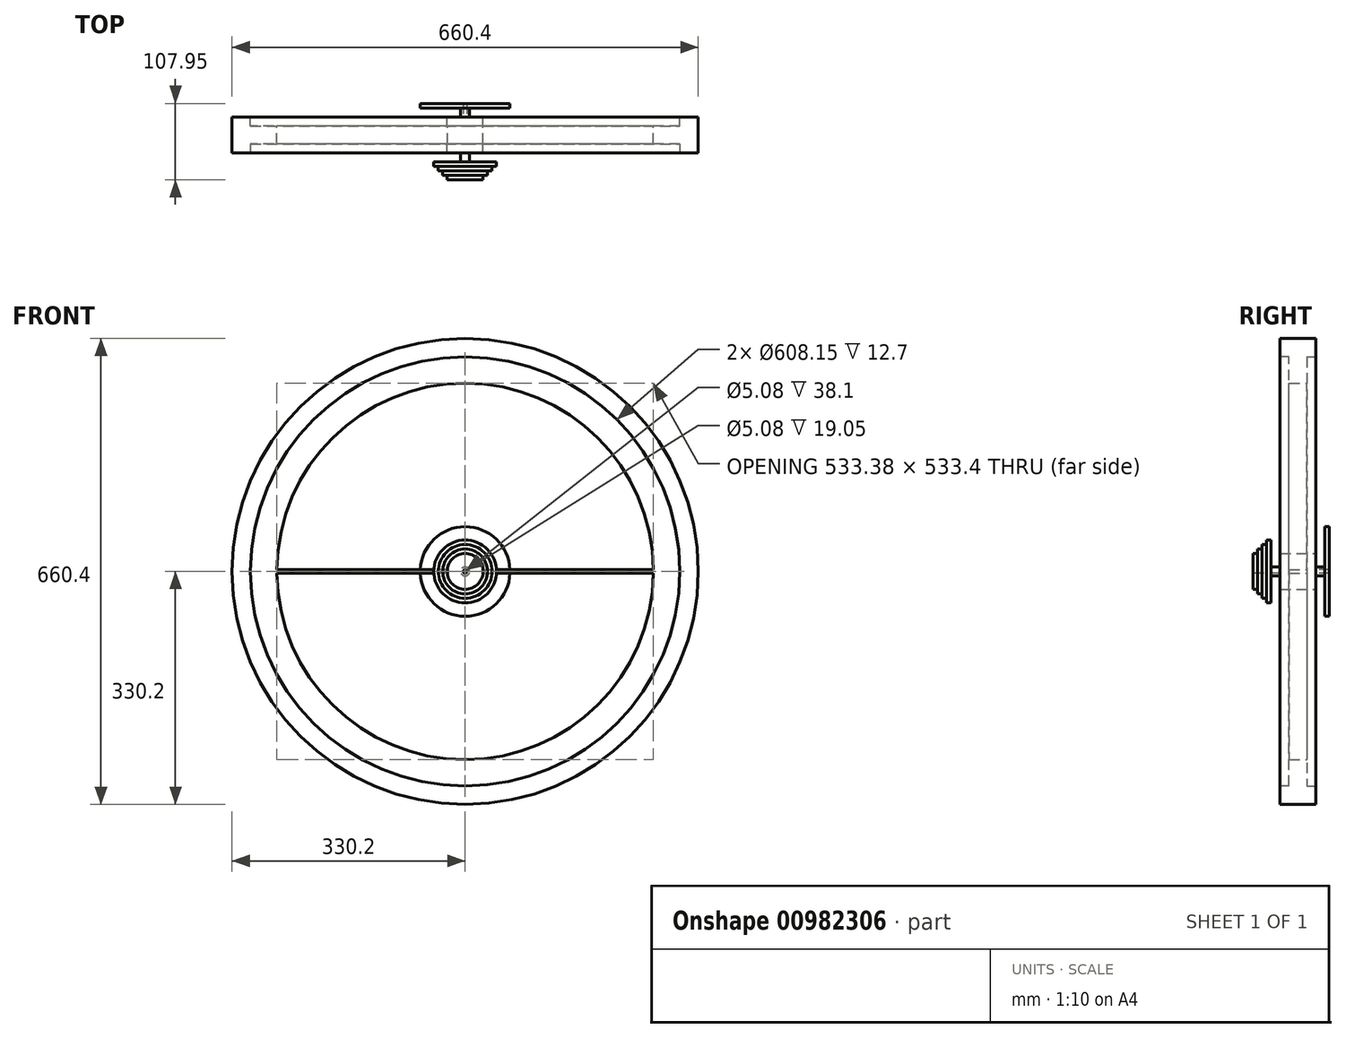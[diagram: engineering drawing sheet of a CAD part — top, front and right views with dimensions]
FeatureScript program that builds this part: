
annotation { "Feature Type Name" : "Feature", "Feature Type Description" : "" }
export const myFeature = defineFeature(function(context is Context, id is Id, definition is map)
    precondition{}
    {
        {
            var Q0;
            Q0=qCreatedBy(makeId("Front.planeOp"),FACE);
            var sketch = newSketch(context, id + "F0", { "sketchPlane" : qUnion([Q0])});
            skCircle(sketch, "E0", {"center": v(0, 0) * mm, "radius": 330.2 * mm});
            skCircle(sketch, "E1", {"center": v(0, 0) * mm, "radius": 266.7 * mm});
            skSolve(sketch);
        }
        {
            var Q0;
            Q0=makeQuery(id+"F0.imprint","IMPRINT",FACE,{"disambiguationData":[TD([[makeQuery(id+"F0.imprint","IMPRINT",EDGE,{"derivedFrom":sQuery(id+"F0.wireOp",EDGE,"E0")}),1.0]])]});
            extrude(context, id + "F1", {"entities" : qUnion([Q0]), "depth" : 25.4 * mm, "offsetDistance" : 25.4 * mm, "hasSecondDirection" : true, "secondDirectionOppositeDirection" : true, "secondDirectionDepth" : 25.4 * mm});
        }
        {
            var Q0;
            Q0=makeQuery(id+"F1.opExtrude","CAP_FACE",FACE,{"disambiguationData":[OSD([sQuery(id+"F0.wireOp",EDGE,"E0"),sQuery(id+"F0.wireOp",EDGE,"E1")])],"isStart":false});
            cPlane(context, id + "F2", {"entities" : qUnion([Q0]), "cplaneType" : CPlaneType.OFFSET, "offset" : 12.7 * mm, "width" : 152.4 * mm, "height" : 152.4 * mm});
        }
        {
            var Q0;
            Q0=qCreatedBy(id+"F2.planeOp",FACE);
            var sketch = newSketch(context, id + "F3", { "sketchPlane" : qUnion([Q0])});
            skPoint(sketch, "E2.0", {"position": v(0, 0) * mm});
            skCircle(sketch, "E3", {"center": v(0, 0) * mm, "radius": 44.45 * mm});
            skCircle(sketch, "E4", {"center": v(0, 0) * mm, "radius": 38.1 * mm});
            skCircle(sketch, "E5", {"center": v(0, 0) * mm, "radius": 31.75 * mm});
            skCircle(sketch, "E6", {"center": v(0, 0) * mm, "radius": 25.4 * mm});
            skCircle(sketch, "E7", {"center": v(0, 0) * mm, "radius": 19.05 * mm});
            skCircle(sketch, "E8", {"center": v(0, 0) * mm, "radius": 6.35 * mm});
            skSolve(sketch);
        }
        {
            var Q0;
            Q0=makeQuery(id+"F3.imprint","IMPRINT",FACE,{"disambiguationData":[TD([[makeQuery(id+"F3.imprint","IMPRINT",EDGE,{"derivedFrom":sQuery(id+"F3.wireOp",EDGE,"E3")}),1.0]])]});
            extrude(context, id + "F4", {"entities" : qUnion([Q0]), "depth" : 6.35 * mm, "offsetDistance" : 25.4 * mm});
        }
        {
            var Q0;
            Q0=makeQuery(id+"F3.imprint","IMPRINT",FACE,{"disambiguationData":[TD([[makeQuery(id+"F3.imprint","IMPRINT",EDGE,{"derivedFrom":sQuery(id+"F3.wireOp",EDGE,"E4")}),1.0]])]});
            extrude(context, id + "F5", {"entities" : qUnion([Q0]), "operationType" : NewBodyOperationType.ADD, "depth" : 12.7 * mm, "offsetDistance" : 25.4 * mm});
        }
        {
            var Q0;
            Q0=makeQuery(id+"F3.imprint","IMPRINT",FACE,{"disambiguationData":[TD([[makeQuery(id+"F3.imprint","IMPRINT",EDGE,{"derivedFrom":sQuery(id+"F3.wireOp",EDGE,"E5")}),1.0]])]});
            extrude(context, id + "F6", {"entities" : qUnion([Q0]), "operationType" : NewBodyOperationType.ADD, "depth" : 19.05 * mm, "offsetDistance" : 25.4 * mm});
        }
        {
            var Q0;
            Q0=makeQuery(id+"F3.imprint","IMPRINT",FACE,{"disambiguationData":[TD([[makeQuery(id+"F3.imprint","IMPRINT",EDGE,{"derivedFrom":sQuery(id+"F3.wireOp",EDGE,"E6")}),1.0]])]});
            extrude(context, id + "F7", {"entities" : qUnion([Q0]), "operationType" : NewBodyOperationType.ADD, "depth" : 25.4 * mm, "offsetDistance" : 25.4 * mm});
        }
        {
            var Q0;
            Q0=makeQuery(id+"F1.opExtrude","CAP_FACE",FACE,{"disambiguationData":[OSD([sQuery(id+"F0.wireOp",EDGE,"E0"),sQuery(id+"F0.wireOp",EDGE,"E1")])],"isStart":true});
            cPlane(context, id + "F8", {"entities" : qUnion([Q0]), "cplaneType" : CPlaneType.OFFSET, "offset" : 12.7 * mm, "width" : 152.4 * mm, "height" : 152.4 * mm});
        }
        {
            var Q0;
            Q0=qCreatedBy(id+"F8.planeOp",FACE);
            var sketch = newSketch(context, id + "F9", { "sketchPlane" : qUnion([Q0])});
            skPoint(sketch, "E9.0", {"position": v(0, 0) * mm});
            skCircle(sketch, "E10", {"center": v(0, 0) * mm, "radius": 63.5 * mm});
            skSolve(sketch);
        }
        {
            var Q0;
            Q0=makeQuery(id+"F9.imprint","IMPRINT",FACE,{"disambiguationData":[TD([[makeQuery(id+"F9.imprint","IMPRINT",EDGE,{"derivedFrom":sQuery(id+"F9.wireOp",EDGE,"E10")}),1.0]])]});
            extrude(context, id + "F10", {"entities" : qUnion([Q0]), "depth" : 6.35 * mm, "offsetDistance" : 25.4 * mm});
        }
        {
            var Q0;
            Q0=makeQuery(id+"F3.imprint","IMPRINT",FACE,{"disambiguationData":[TD([[makeQuery(id+"F3.imprint","IMPRINT",EDGE,{"derivedFrom":sQuery(id+"F3.wireOp",EDGE,"E8")}),1.0]])]});
            extrude(context, id + "F11", {"entities" : qUnion([Q0]), "operationType" : NewBodyOperationType.ADD, "depth" : 25.4 * mm, "offsetDistance" : 25.4 * mm, "hasSecondDirection" : true, "secondDirectionOppositeDirection" : true, "secondDirectionDepth" : 76.2 * mm});
        }
        {
            var Q0;
            Q0=makeQuery(id+"F7.opExtrude","CAP_FACE",FACE,{"disambiguationData":[OSD([sQuery(id+"F3.wireOp",EDGE,"E6"),sQuery(id+"F3.wireOp",EDGE,"E7")])],"isStart":false});
            var sketch = newSketch(context, id + "F12", { "sketchPlane" : qUnion([Q0])});
            skCircle(sketch, "E11", {"center": v(0, 0) * mm, "radius": 20.6 * mm});
            skCircle(sketch, "E12", {"center": v(0, 0) * mm, "radius": 2.54 * mm});
            skSolve(sketch);
        }
        {
            var Q0;
            Q0=makeQuery(id+"F12.imprint","IMPRINT",FACE,{"disambiguationData":[TD([[makeQuery(id+"F12.imprint","IMPRINT",EDGE,{"derivedFrom":makeQuery(id+"F7.opExtrude","CAP_EDGE",EDGE,{"disambiguationData":[OSD([sQuery(id+"F3.wireOp",EDGE,"E7")])],"isStart":false})}),1.0]])]});
            extrude(context, id + "F13", {"entities" : qUnion([Q0]), "operationType" : NewBodyOperationType.ADD, "oppositeDirection" : true, "depth" : 25.4 * mm, "offsetDistance" : 25.4 * mm});
        }
        {
            var Q0;
            Q0=makeQuery(id+"F12.imprint","IMPRINT",FACE,{"disambiguationData":[TD([[makeQuery(id+"F12.imprint","IMPRINT",EDGE,{"derivedFrom":sQuery(id+"F12.wireOp",EDGE,"E12")}),1.0]])]});
            extrude(context, id + "F14", {"entities" : qUnion([Q0]), "operationType" : NewBodyOperationType.REMOVE, "endBound" : BoundingType.THROUGH_ALL, "oppositeDirection" : true, "depth" : 25.4 * mm, "offsetDistance" : 25.4 * mm});
        }
        {
            var Q0;
            Q0=qCreatedBy(makeId("Front.planeOp"),FACE);
            var sketch = newSketch(context, id + "F15", { "sketchPlane" : qUnion([Q0])});
            skPoint(sketch, "E13.0", {"position": v(0, 0) * mm});
            skCircle(sketch, "E13.1", {"center": v(0, 0) * mm, "radius": 2.54 * mm});
            skCircle(sketch, "E14", {"center": v(0, 0) * mm, "radius": 6.35 * mm});
            skLineSegment(sketch, "E15.bottom", {"start": v(0, 2.54) * mm, "end": v(304.8, 2.54) * mm});
            skLineSegment(sketch, "E15.top", {"start": v(0, -2.54) * mm, "end": v(304.8, -2.54) * mm});
            skLineSegment(sketch, "E15.left", {"start": v(0, 2.54) * mm, "end": v(0, -2.54) * mm});
            skLineSegment(sketch, "E15.right", {"start": v(304.8, 2.54) * mm, "end": v(304.8, -2.54) * mm});
            skLineSegment(sketch, "E16.bottom", {"start": v(0, 2.54) * mm, "end": v(-304.8, 2.54) * mm});
            skLineSegment(sketch, "E16.top", {"start": v(0, -2.54) * mm, "end": v(-304.8, -2.54) * mm});
            skLineSegment(sketch, "E16.right", {"start": v(-304.8, 2.54) * mm, "end": v(-304.8, -2.54) * mm});
            skSolve(sketch);
        }
        {
            var Q0;
            {var subQ5=sQuery(id+"F15.wireOp",EDGE,"E15.right");Q0=makeQuery(id+"F15.imprint","IMPRINT",FACE,{"disambiguationData":[TD([[makeQuery(id+"F15.imprint","IMPRINT",EDGE,{"derivedFrom":subQ5}),-1.0]])]});}
            var Q1;
            {var subQ5=sQuery(id+"F15.wireOp",EDGE,"E16.right");Q1=makeQuery(id+"F15.imprint","IMPRINT",FACE,{"disambiguationData":[TD([[makeQuery(id+"F15.imprint","IMPRINT",EDGE,{"derivedFrom":subQ5}),1.0]])]});}
            extrude(context, id + "F16", {"entities" : qUnion([Q0, Q1]), "operationType" : NewBodyOperationType.ADD, "depth" : 12.7 * mm, "offsetDistance" : 25.4 * mm, "hasSecondDirection" : true, "secondDirectionOppositeDirection" : true, "secondDirectionDepth" : 12.7 * mm});
        }
        {
            var Q0;
            Q0=makeQuery(id+"F12.imprint","IMPRINT",FACE,{"disambiguationData":[TD([[makeQuery(id+"F12.imprint","IMPRINT",EDGE,{"derivedFrom":sQuery(id+"F12.wireOp",EDGE,"E12")}),1.0]])]});
            extrude(context, id + "F17", {"entities" : qUnion([Q0]), "operationType" : NewBodyOperationType.REMOVE, "endBound" : BoundingType.THROUGH_ALL, "oppositeDirection" : true, "depth" : 25.4 * mm, "offsetDistance" : 25.4 * mm});
        }
        {
            var Q0;
            Q0=qCreatedBy(makeId("Front.planeOp"),FACE);
            var sketch = newSketch(context, id + "F18", { "sketchPlane" : qUnion([Q0])});
            skPoint(sketch, "E17.0", {"position": v(0, 0) * mm});
            skCircle(sketch, "E18", {"center": v(0, 0) * mm, "radius": 25.4 * mm});
            skSolve(sketch);
        }
        {
            var Q0;
            Q0=makeQuery(id+"F18.imprint","IMPRINT",FACE,{"disambiguationData":[TD([[makeQuery(id+"F18.imprint","IMPRINT",EDGE,{"derivedFrom":sQuery(id+"F18.wireOp",EDGE,"E18")}),1.0]])]});
            extrude(context, id + "F19", {"entities" : qUnion([Q0]), "operationType" : NewBodyOperationType.ADD, "depth" : 25.4 * mm, "offsetDistance" : 25.4 * mm, "hasSecondDirection" : true, "secondDirectionOppositeDirection" : true, "secondDirectionDepth" : 25.4 * mm});
        }
        {
            var Q0;
            Q0=makeQuery(id+"F1.opExtrude","CAP_FACE",FACE,{"disambiguationData":[OSD([sQuery(id+"F0.wireOp",EDGE,"E0"),sQuery(id+"F0.wireOp",EDGE,"E1")])],"isStart":false});
            var sketch = newSketch(context, id + "F20", { "sketchPlane" : qUnion([Q0])});
            skPoint(sketch, "E19.0", {"position": v(0, 0) * mm});
            skCircle(sketch, "E20", {"center": v(0, 0) * mm, "radius": 304.08 * mm});
            skSolve(sketch);
        }
        {
            var Q0;
            Q0=makeQuery(id+"F20.imprint","IMPRINT",FACE,{"disambiguationData":[TD([[makeQuery(id+"F20.imprint","IMPRINT",EDGE,{"derivedFrom":sQuery(id+"F20.wireOp",EDGE,"E20")}),1.0]])]});
            extrude(context, id + "F21", {"entities" : qUnion([Q0]), "operationType" : NewBodyOperationType.REMOVE, "oppositeDirection" : true, "depth" : 12.7 * mm, "offsetDistance" : 25.4 * mm});
        }
        {
            var Q0;
            Q0=makeQuery(id+"F1.opExtrude","CAP_FACE",FACE,{"disambiguationData":[OSD([sQuery(id+"F0.wireOp",EDGE,"E0"),sQuery(id+"F0.wireOp",EDGE,"E1")])],"isStart":true});
            var sketch = newSketch(context, id + "F22", { "sketchPlane" : qUnion([Q0])});
            skPoint(sketch, "E21.0", {"position": v(0, 0) * mm});
            skCircle(sketch, "E22", {"center": v(0, 0) * mm, "radius": 304.08 * mm});
            skSolve(sketch);
        }
        {
            var Q0;
            Q0=makeQuery(id+"F22.imprint","IMPRINT",FACE,{"disambiguationData":[TD([[makeQuery(id+"F22.imprint","IMPRINT",EDGE,{"derivedFrom":sQuery(id+"F22.wireOp",EDGE,"E22")}),1.0]])]});
            extrude(context, id + "F23", {"entities" : qUnion([Q0]), "operationType" : NewBodyOperationType.REMOVE, "oppositeDirection" : true, "depth" : 12.7 * mm, "offsetDistance" : 25.4 * mm});
        }
    });
